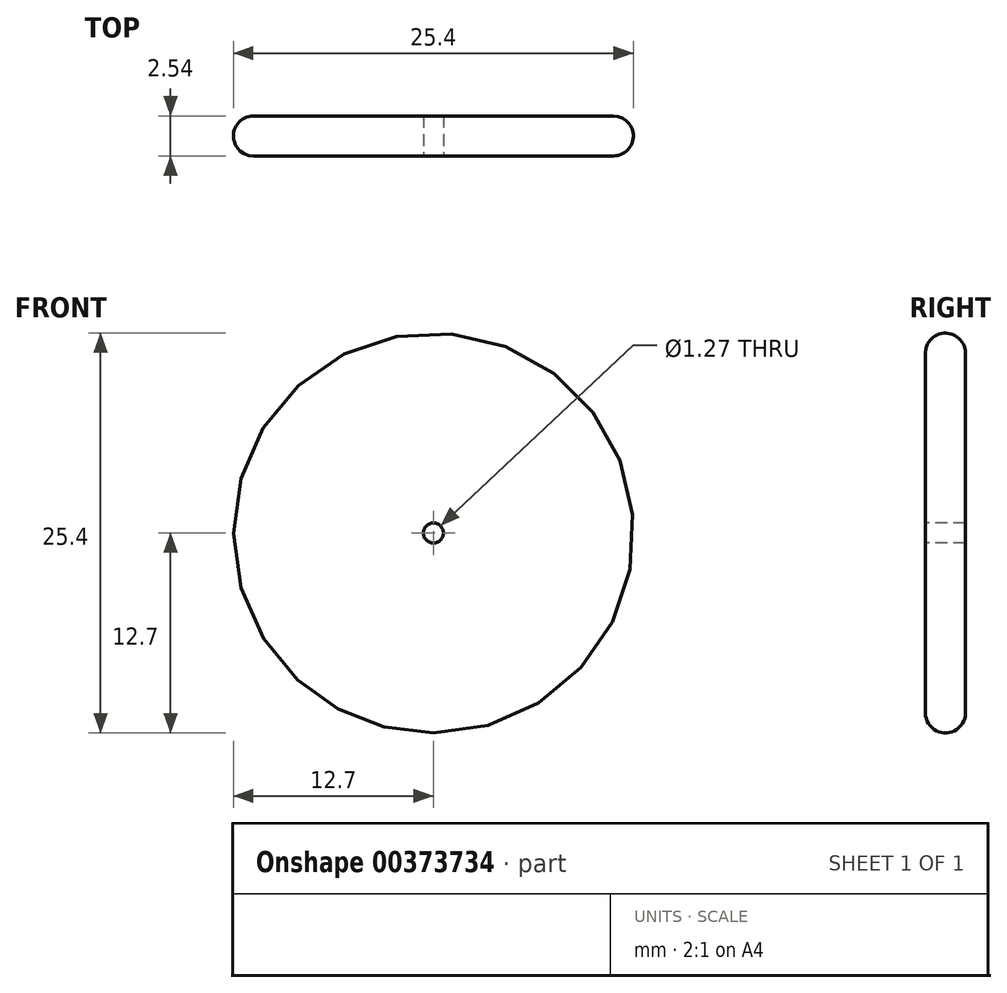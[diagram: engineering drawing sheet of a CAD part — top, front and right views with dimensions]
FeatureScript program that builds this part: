
annotation { "Feature Type Name" : "Feature", "Feature Type Description" : "" }
export const myFeature = defineFeature(function(context is Context, id is Id, definition is map)
    precondition{}
    {
        {
            var Q0;
            Q0=qCreatedBy(makeId("Front.planeOp"),FACE);
            var sketch = newSketch(context, id + "F0", { "sketchPlane" : qUnion([Q0])});
            skCircle(sketch, "E0", {"center": v(0, 0) * mm, "radius": 12.7 * mm});
            skSolve(sketch);
        }
        {
            var Q0;
            Q0 = qSketchRegion(id + "F0", true);
            extrude(context, id + "F1", {"entities" : qUnion([Q0]), "depth" : 2.54 * mm});
        }
        {
            var Q0;
            Q0=makeQuery(id+"F1.opExtrude","CAP_FACE",FACE,{"disambiguationData":[OSD([sQuery(id+"F0.wireOp",EDGE,"E0")])],"isStart":false});
            var sketch = newSketch(context, id + "F2", { "sketchPlane" : qUnion([Q0])});
            skCircle(sketch, "E1", {"center": v(0, 0) * mm, "radius": 0.64 * mm});
            skSolve(sketch);
        }
        {
            var Q0;
            Q0=makeQuery(id+"F2.imprint","IMPRINT",FACE,{"disambiguationData":[TD([[makeQuery(id+"F2.imprint","IMPRINT",EDGE,{"derivedFrom":sQuery(id+"F2.wireOp",EDGE,"E1")}),1.0]])]});
            extrude(context, id + "F3", {"entities" : qUnion([Q0]), "operationType" : NewBodyOperationType.REMOVE, "oppositeDirection" : true, "depth" : 25.4 * mm});
        }
        {
            var Q0;
            Q0=makeQuery(id+"F1.opExtrude","CAP_EDGE",EDGE,{"disambiguationData":[OSD([sQuery(id+"F0.wireOp",EDGE,"E0")])],"isStart":false});
            var Q1;
            Q1=makeQuery(id+"F1.opExtrude","CAP_EDGE",EDGE,{"disambiguationData":[OSD([sQuery(id+"F0.wireOp",EDGE,"E0")])],"isStart":true});
            fillet(context, id + "F4", {"entities" : qUnion([Q0, Q1]), "radius" : 1.27 * mm, "tangentPropagation" : true, "allowEdgeOverflow" : false});
        }
    });
